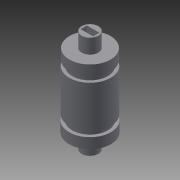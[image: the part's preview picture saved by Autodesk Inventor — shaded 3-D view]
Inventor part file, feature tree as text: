
AUTODESK INVENTOR PART (.ipt)
format: ipt  version: 2015 (Build 190159000, 159)  size: 156,672 bytes
history: native  units: mm
features: extrude x11, sketch x11
ambient origin geometry x8: Origin, YZ Plane, XZ Plane, XY Plane, X Axis, Y Axis, Z Axis, Center Point
bodies: Solid1 (feature_tree)
feature tree (22):
  extrude  "Extrusion1"  Depth=5.0mm TaperAngle=0.0deg
  extrude  "Extrusion2"  Depth=3.0mm
  extrude  "Extrusion3"  Depth=2.5mm
  extrude  "Extrusion4"  Depth=2.5mm
  extrude  "Extrusion5"  Depth=2.5mm TaperAngle=0.0deg
  extrude  "Extrusion6"  Depth=2.5mm TaperAngle=0.0deg
  extrude  "Extrusion7"  Depth=2.5mm TaperAngle=0.0deg
  extrude  "Extrusion8"  Depth=5.0mm
  extrude  "Extrusion9"  Depth=3.0mm
  extrude  "Extrusion10"  Depth=3.0mm
  extrude  "Extrusion11"  Depth=7.0mm
  sketch  "Sketch1"  dims[d0=20.0mm d1=5.0mm d2=0.0mm]
  sketch  "Sketch2"  dims[d3=17.0mm d4=3.0mm]
  sketch  "Sketch3"  dims[d5=2.5mm d6=0.0mm d7=2.5mm]
  sketch  "Sketch4"  dims[d8=2.5mm d9=0.0mm d10=8.408088mm]
  sketch  "Sketch5"  dims[d11=1.0mm d12=2.5mm d13=0.0mm]
  sketch  "Sketch6"  dims[d14=20.0mm d15=0.0mm d16=2.5mm d17=0.0mm]
  sketch  "Sketch7"  dims[d18=2.5mm d19=0.0mm d20=2.5mm d21=0.0mm]
  sketch  "Sketch8"  dims[d22=5.0mm d23=0.0mm d24=8.0mm]
  sketch  "Sketch9"  dims[d25=6.0mm d26=3.0mm]
  sketch  "Sketch10"  dims[d27=1.5mm d28=3.0mm]
  sketch  "Sketch11"  dims[d29=7.0mm d30=0.0mm d31=8.0mm d32=7.0mm d33=0.0mm]
